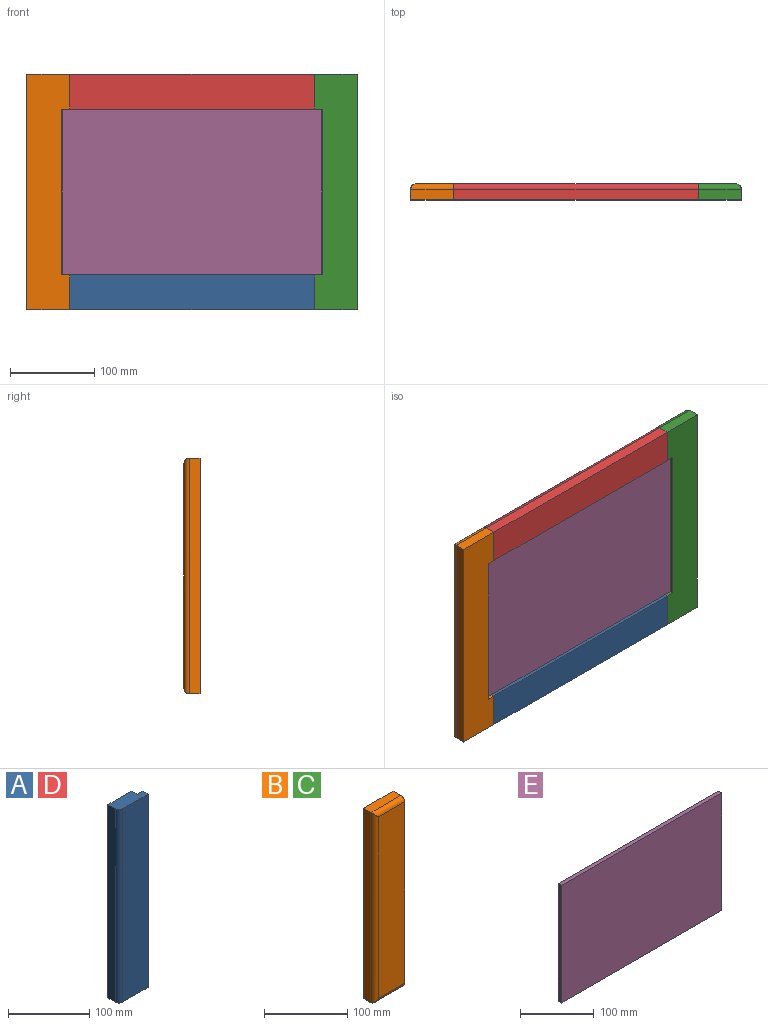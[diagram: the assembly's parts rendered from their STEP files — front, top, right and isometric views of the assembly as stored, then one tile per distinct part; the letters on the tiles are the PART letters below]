
ASSEMBLY  parts=5 mates=4
PART A: 9 faces, bbox 50.8x19.1x290.5 mm
  f0: plane 50.8x19.05mm, normal (0,0,1), area 868.4mm2, adj f2,f3,f4,f5,f6,f7,f8
  f1: plane 50.8x19.05mm, normal (0,0,-1), area 868.4mm2, adj f2,f3,f4,f5,f6,f7,f8
  f2: plane 290.51x12.7mm, normal (-1,0,0), area 3689.5mm2, adj f0,f1,f5,f6
  f3: plane 290.51x44.45mm, normal (0,-1,0), area 12913.3mm2, adj f0,f1,f4,f6
  f4: plane 290.51x9.53mm, normal (1,0,0), area 2767.1mm2, adj f0,f1,f3,f7
  f5: plane 290.51x41.28mm, normal (0,1,0), area 11990.9mm2, adj f0,f1,f2,f8
  f6: cylinder r=6.35mm len=290.51mm, axis (0,0,1), area 2897.7mm2, adj f0,f1,f2,f3
  f7: plane 290.51x9.53mm, normal (0,1,0), area 2767.1mm2, adj f0,f1,f4,f8
  f8: plane 290.51x9.53mm, normal (1,0,0), area 2767.1mm2, adj f0,f1,f5,f7
PART B: 13 faces, bbox 50.8x19.1x279.4 mm
  f0: plane 279.4x19.05mm, normal (1,0,0), area 3430.3mm2, adj f1,f3,f4,f5,f6,f7,f9,f10
  f1: plane 279.4x50.8mm, normal (0,1,0), area 12318.5mm2, adj f0,f2,f4,f5,f9,f10,f11
  f2: plane 279.4x12.7mm, normal (-1,0,0), area 3548.4mm2, adj f1,f4,f5,f8
  f3: plane 266.7x44.45mm, normal (0,-1,0), area 11854.8mm2, adj f0,f6,f7,f8
  f4: plane 50.8x12.7mm, normal (0,0,1), area 645.2mm2, adj f0,f1,f2,f6
  f5: plane 50.8x12.7mm, normal (0,0,-1), area 645.2mm2, adj f0,f1,f2,f7
  f6: cylinder r=6.35mm len=50.8mm, axis (-1,0,0), area 483.7mm2, adj f0,f3,f4,f8
  f7: cylinder r=6.35mm len=50.8mm, axis (1,0,0), area 483.7mm2, adj f0,f3,f5,f8
  f8: cylinder r=6.35mm len=279.4mm, axis (0,0,1), area 2740.9mm2, adj f2,f3,f6,f7
  f9: plane 9.53x9.53mm, normal (0,0,1), area 90.7mm2, adj f0,f1,f11,f12
  f10: plane 9.53x9.53mm, normal (0,0,-1), area 90.7mm2, adj f0,f1,f11,f12
  f11: plane 196.85x9.53mm, normal (1,0,0), area 1875mm2, adj f1,f9,f10,f12
  f12: plane 196.85x9.53mm, normal (0,1,0), area 1875mm2, adj f0,f9,f10,f11
PART C: same geometry as B
PART D: same geometry as A
PART E: 6 faces, bbox 308x6.4x195.3 mm
  f0: plane 195.26x6.35mm, normal (-1,0,0), area 1239.9mm2, adj f1,f3,f4,f5
  f1: plane 307.98x6.35mm, normal (0,0,-1), area 1955.6mm2, adj f0,f2,f4,f5
  f2: plane 195.26x6.35mm, normal (1,0,0), area 1239.9mm2, adj f1,f3,f4,f5
  f3: plane 307.98x6.35mm, normal (0,0,1), area 1955.6mm2, adj f0,f2,f4,f5
  f4: plane 307.98x195.26mm, normal (0,-1,0), area 60136mm2, adj f0,f1,f2,f3
  f5: plane 307.98x195.26mm, normal (0,1,0), area 60136mm2, adj f0,f1,f2,f3
PLACE A rot(axis=(-0.71,0,-0.71),180deg) t=(-312.74,0,-139.7)mm
PLACE B rot(axis=(-1,0,0),180deg) t=(-363.54,0,139.7)mm
PLACE C rot(axis=(0,0,1),180deg) t=(28.58,0,-139.7)mm
PLACE D rot(axis=(-0.71,0,0.71),180deg) t=(-22.23,0,139.7)mm
PLACE E rot(axis=(0,0,1),180deg) t=(-13.49,-15.88,-97.63)mm
MATE fastened C.f4 <-> D.f2  axis (0,0,1) through (-22.23,-12.7,139.7)mm
MATE fastened D.f0 <-> B.f0  axis (-1,0,0) through (-312.74,-19.05,139.7)mm
MATE fastened B.f0 <-> A.f1  axis (1,0,0) through (-312.74,-19.05,-139.7)mm
MATE fastened E.f4 <-> C.f12  axis (0,1,0) through (-13.49,-9.53,97.63)mm
